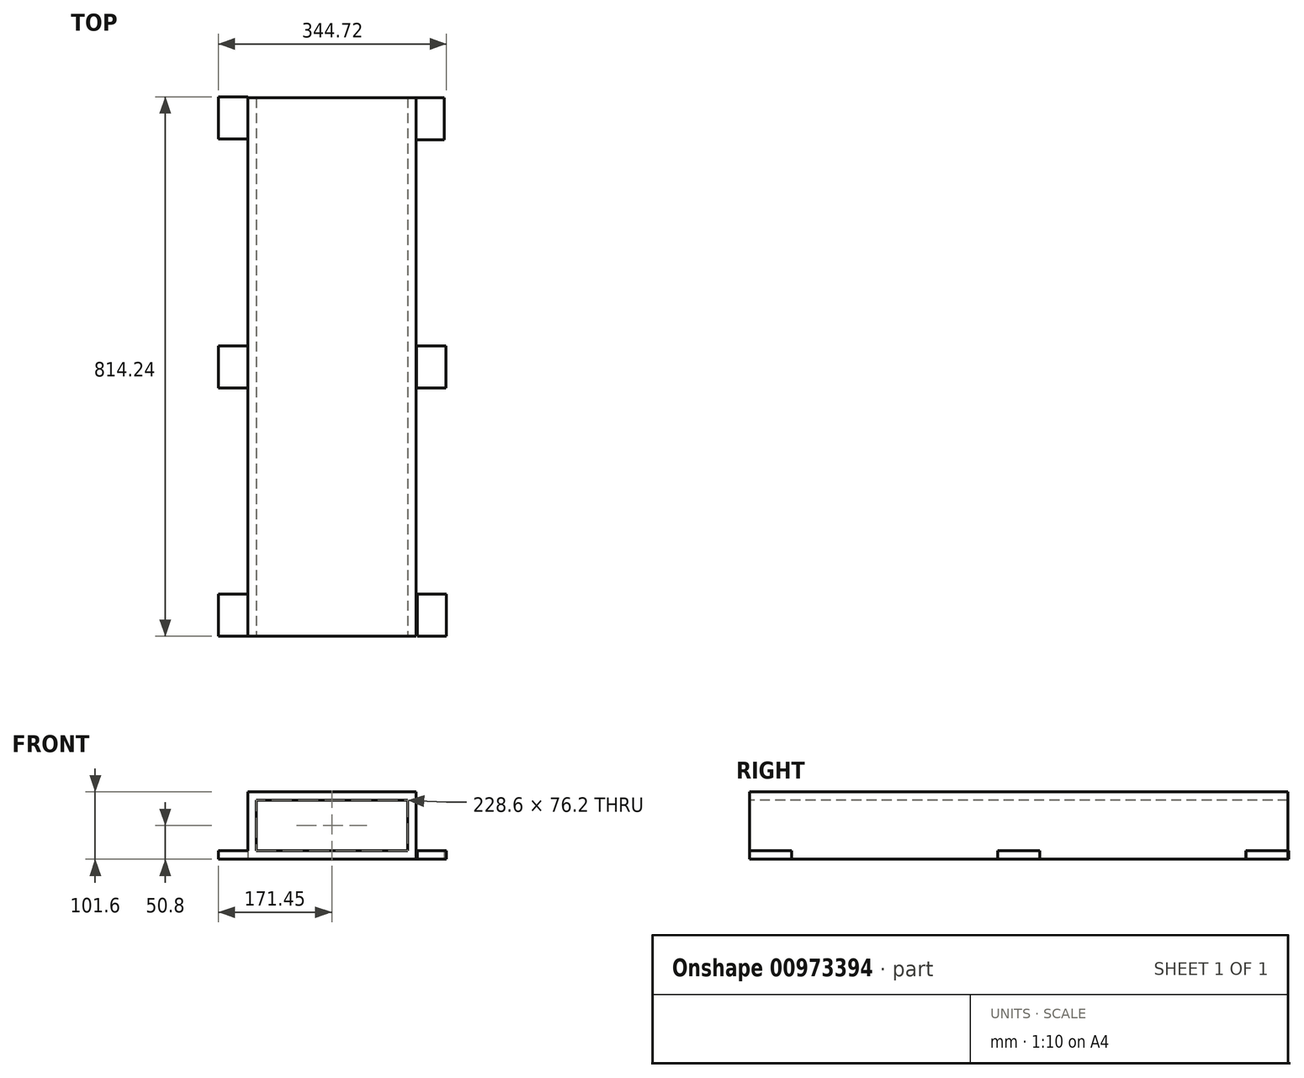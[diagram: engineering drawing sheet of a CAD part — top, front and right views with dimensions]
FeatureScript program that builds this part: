
annotation { "Feature Type Name" : "Feature", "Feature Type Description" : "" }
export const myFeature = defineFeature(function(context is Context, id is Id, definition is map)
    precondition{}
    {
        {
            var Q0;
            Q0=qCreatedBy(makeId("Front.planeOp"),FACE);
            var sketch = newSketch(context, id + "F0", { "sketchPlane" : qUnion([Q0])});
            skLineSegment(sketch, "E0.bottom", {"start": v(0, 0) * mm, "end": v(254, 0) * mm});
            skLineSegment(sketch, "E0.top", {"start": v(0, 101.6) * mm, "end": v(254, 101.6) * mm});
            skLineSegment(sketch, "E0.left", {"start": v(0, 0) * mm, "end": v(0, 101.6) * mm});
            skLineSegment(sketch, "E0.right", {"start": v(254, 0) * mm, "end": v(254, 101.6) * mm});
            skLineSegment(sketch, "E1.bottom", {"start": v(241.3, 88.9) * mm, "end": v(12.7, 88.9) * mm});
            skLineSegment(sketch, "E1.top", {"start": v(241.3, 12.7) * mm, "end": v(12.7, 12.7) * mm});
            skLineSegment(sketch, "E1.left", {"start": v(241.3, 88.9) * mm, "end": v(241.3, 12.7) * mm});
            skLineSegment(sketch, "E1.right", {"start": v(12.7, 88.9) * mm, "end": v(12.7, 12.7) * mm});
            skPoint(sketch, "E1.middle", {"position": v(127, 50.8) * mm});
            skSolve(sketch);
        }
        {
            var Q0;
            Q0=makeQuery(id+"F0.imprint","IMPRINT",FACE,{"disambiguationData":[TD([[makeQuery(id+"F0.imprint","IMPRINT",EDGE,{"derivedFrom":sQuery(id+"F0.wireOp",EDGE,"E0.bottom")}),1.0]])]});
            extrude(context, id + "F1", {"entities" : qUnion([Q0]), "depth" : -812.8 * mm, "offsetDistance" : 25.4 * mm});
        }
        {
            var Q0;
            Q0=qCreatedBy(makeId("Top.planeOp"),FACE);
            var sketch = newSketch(context, id + "F2", { "sketchPlane" : qUnion([Q0])});
            skLineSegment(sketch, "E2.bottom", {"start": v(0, 0) * mm, "end": v(-44.45, 0) * mm});
            skLineSegment(sketch, "E2.top", {"start": v(0, 63.5) * mm, "end": v(-44.45, 63.5) * mm});
            skLineSegment(sketch, "E2.left", {"start": v(0, 0) * mm, "end": v(0, 63.5) * mm});
            skLineSegment(sketch, "E2.right", {"start": v(-44.45, 0) * mm, "end": v(-44.45, 63.5) * mm});
            skLineSegment(sketch, "E3.bottom", {"start": v(255.82, 0) * mm, "end": v(300.27, 0) * mm});
            skLineSegment(sketch, "E3.top", {"start": v(255.82, 63.5) * mm, "end": v(300.27, 63.5) * mm});
            skLineSegment(sketch, "E3.left", {"start": v(255.82, 0) * mm, "end": v(255.82, 63.5) * mm});
            skLineSegment(sketch, "E3.right", {"start": v(300.27, 0) * mm, "end": v(300.27, 63.5) * mm});
            skLineSegment(sketch, "E4.bottom", {"start": v(736.3, 82.6) * mm, "end": v(675.47, 82.6) * mm});
            skLineSegment(sketch, "E4.top", {"start": v(736.3, 72.02) * mm, "end": v(675.47, 72.02) * mm});
            skLineSegment(sketch, "E4.left", {"start": v(736.3, 82.6) * mm, "end": v(736.3, 72.02) * mm});
            skLineSegment(sketch, "E4.right", {"start": v(675.47, 82.6) * mm, "end": v(675.47, 72.02) * mm});
            skLineSegment(sketch, "E5.bottom", {"start": v(0, 814.24) * mm, "end": v(-44.45, 814.24) * mm});
            skLineSegment(sketch, "E5.top", {"start": v(0, 750.74) * mm, "end": v(-44.45, 750.74) * mm});
            skLineSegment(sketch, "E5.left", {"start": v(0, 814.24) * mm, "end": v(0, 750.74) * mm});
            skLineSegment(sketch, "E5.right", {"start": v(-44.45, 814.24) * mm, "end": v(-44.45, 750.74) * mm});
            skLineSegment(sketch, "E6.bottom", {"start": v(252.38, 812.8) * mm, "end": v(296.83, 812.8) * mm});
            skLineSegment(sketch, "E6.top", {"start": v(252.38, 749.3) * mm, "end": v(296.83, 749.3) * mm});
            skLineSegment(sketch, "E6.left", {"start": v(252.38, 812.8) * mm, "end": v(252.38, 749.3) * mm});
            skLineSegment(sketch, "E6.right", {"start": v(296.83, 812.8) * mm, "end": v(296.83, 749.3) * mm});
            skLineSegment(sketch, "E7.bottom", {"start": v(255.01, 438.15) * mm, "end": v(299.46, 438.15) * mm});
            skLineSegment(sketch, "E7.top", {"start": v(255.01, 374.65) * mm, "end": v(299.46, 374.65) * mm});
            skLineSegment(sketch, "E7.left", {"start": v(255.01, 438.15) * mm, "end": v(255.01, 374.65) * mm});
            skLineSegment(sketch, "E7.right", {"start": v(299.46, 438.15) * mm, "end": v(299.46, 374.65) * mm});
            skLineSegment(sketch, "E8.bottom", {"start": v(0, 438.15) * mm, "end": v(-44.45, 438.15) * mm});
            skLineSegment(sketch, "E8.top", {"start": v(0, 374.65) * mm, "end": v(-44.45, 374.65) * mm});
            skLineSegment(sketch, "E8.left", {"start": v(0, 438.15) * mm, "end": v(0, 374.65) * mm});
            skLineSegment(sketch, "E8.right", {"start": v(-44.45, 438.15) * mm, "end": v(-44.45, 374.65) * mm});
            skSolve(sketch);
        }
        {
            var Q0;
            Q0=makeQuery(id+"F2.imprint","IMPRINT",FACE,{"disambiguationData":[TD([[makeQuery(id+"F2.imprint","IMPRINT",EDGE,{"derivedFrom":sQuery(id+"F2.wireOp",EDGE,"E5.bottom")}),1.0]])]});
            var Q1;
            Q1=makeQuery(id+"F2.imprint","IMPRINT",FACE,{"disambiguationData":[TD([[makeQuery(id+"F2.imprint","IMPRINT",EDGE,{"derivedFrom":sQuery(id+"F2.wireOp",EDGE,"E6.bottom")}),-1.0]])]});
            var Q2;
            Q2=makeQuery(id+"F2.imprint","IMPRINT",FACE,{"disambiguationData":[TD([[makeQuery(id+"F2.imprint","IMPRINT",EDGE,{"derivedFrom":sQuery(id+"F2.wireOp",EDGE,"E7.bottom")}),-1.0]])]});
            var Q3;
            Q3=makeQuery(id+"F2.imprint","IMPRINT",FACE,{"disambiguationData":[TD([[makeQuery(id+"F2.imprint","IMPRINT",EDGE,{"derivedFrom":sQuery(id+"F2.wireOp",EDGE,"E8.bottom")}),1.0]])]});
            var Q4;
            Q4=makeQuery(id+"F2.imprint","IMPRINT",FACE,{"disambiguationData":[TD([[makeQuery(id+"F2.imprint","IMPRINT",EDGE,{"derivedFrom":sQuery(id+"F2.wireOp",EDGE,"E2.bottom")}),-1.0]])]});
            var Q5;
            Q5=makeQuery(id+"F2.imprint","IMPRINT",FACE,{"disambiguationData":[TD([[makeQuery(id+"F2.imprint","IMPRINT",EDGE,{"derivedFrom":sQuery(id+"F2.wireOp",EDGE,"E3.bottom")}),1.0]])]});
            extrude(context, id + "F3", {"entities" : qUnion([Q0, Q1, Q2, Q3, Q4, Q5]), "operationType" : NewBodyOperationType.ADD, "depth" : 12.7 * mm, "offsetDistance" : 25.4 * mm});
        }
    });
